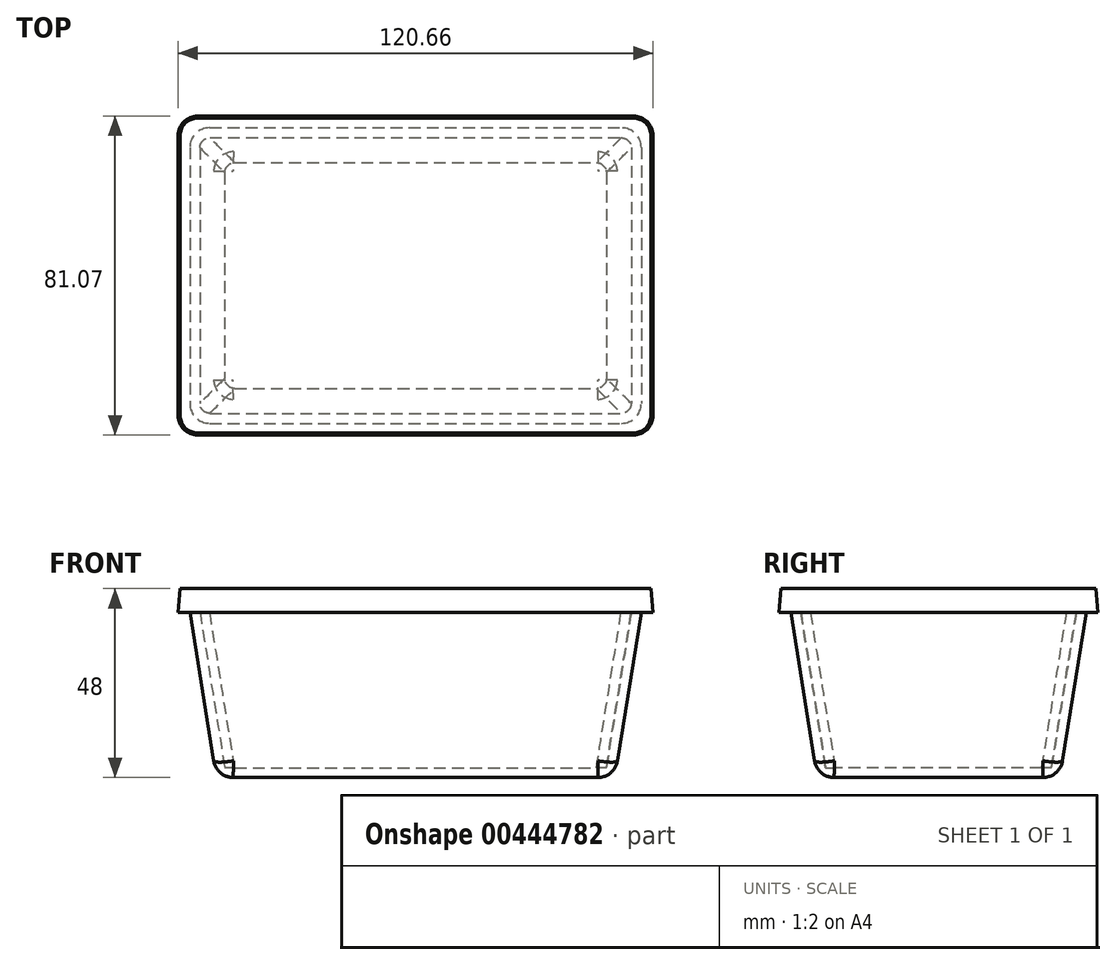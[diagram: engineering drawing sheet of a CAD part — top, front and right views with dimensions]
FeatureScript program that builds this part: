
annotation { "Feature Type Name" : "Feature", "Feature Type Description" : "" }
export const myFeature = defineFeature(function(context is Context, id is Id, definition is map)
    precondition{}
    {
        {
            var Q0;
            Q0=qCreatedBy(makeId("Top.planeOp"),FACE);
            var sketch = newSketch(context, id + "F0", { "sketchPlane" : qUnion([Q0])});
            skLineSegment(sketch, "E0.bottom", {"start": v(-49.28, 19.44) * mm, "end": v(41.94, 19.44) * mm});
            skLineSegment(sketch, "E0.top", {"start": v(-49.28, -42.19) * mm, "end": v(41.94, -42.19) * mm});
            skLineSegment(sketch, "E0.left", {"start": v(-54.28, 14.44) * mm, "end": v(-54.28, -37.19) * mm});
            skLineSegment(sketch, "E0.right", {"start": v(46.94, 14.44) * mm, "end": v(46.94, -37.19) * mm});
            skPoint(sketch, "E1.visualSharp", {"position": v(-54.28, 19.44) * mm});
            skArc(sketch, "E1.filletArc", {"start": v(-49.28, 19.44) * mm, "mid": v(-52.81, 17.98) * mm, "end": v(-54.28, 14.44) * mm});
            skPoint(sketch, "E2.visualSharp", {"position": v(-54.28, -42.19) * mm});
            skArc(sketch, "E2.filletArc", {"start": v(-54.28, -37.19) * mm, "mid": v(-52.81, -40.72) * mm, "end": v(-49.28, -42.19) * mm});
            skPoint(sketch, "E3.visualSharp", {"position": v(46.94, -42.19) * mm});
            skArc(sketch, "E3.filletArc", {"start": v(41.94, -42.19) * mm, "mid": v(45.48, -40.72) * mm, "end": v(46.94, -37.19) * mm});
            skPoint(sketch, "E4.visualSharp", {"position": v(46.94, 19.44) * mm});
            skArc(sketch, "E4.filletArc", {"start": v(46.94, 14.44) * mm, "mid": v(45.48, 17.98) * mm, "end": v(41.94, 19.44) * mm});
            skSolve(sketch);
        }
        {
            var Q0;
            Q0=qCreatedBy(makeId("Top.planeOp"),FACE);
            cPlane(context, id + "F1", {"entities" : qUnion([Q0]), "cplaneType" : CPlaneType.OFFSET, "offset" : 42 * mm, "width" : 150 * mm, "height" : 150 * mm});
        }
        {
            var Q0;
            Q0=qCreatedBy(id+"F1.planeOp",FACE);
            var sketch = newSketch(context, id + "F2", { "sketchPlane" : qUnion([Q0])});
            skLineSegment(sketch, "E5.bottom", {"start": v(-56, 26.16) * mm, "end": v(48.66, 26.16) * mm});
            skLineSegment(sketch, "E5.top", {"start": v(-56, -48.9) * mm, "end": v(48.66, -48.9) * mm});
            skLineSegment(sketch, "E5.left", {"start": v(-61, 21.16) * mm, "end": v(-61, -43.9) * mm});
            skLineSegment(sketch, "E5.right", {"start": v(53.66, 21.16) * mm, "end": v(53.66, -43.9) * mm});
            skPoint(sketch, "E6.visualSharp", {"position": v(-61, 26.16) * mm});
            skArc(sketch, "E6.filletArc", {"start": v(-56, 26.16) * mm, "mid": v(-59.53, 24.7) * mm, "end": v(-61, 21.16) * mm});
            skPoint(sketch, "E7.visualSharp", {"position": v(-61, -48.9) * mm});
            skArc(sketch, "E7.filletArc", {"start": v(-61, -43.9) * mm, "mid": v(-59.53, -47.44) * mm, "end": v(-56, -48.9) * mm});
            skPoint(sketch, "E8.visualSharp", {"position": v(53.66, -48.9) * mm});
            skArc(sketch, "E8.filletArc", {"start": v(48.66, -48.9) * mm, "mid": v(52.2, -47.44) * mm, "end": v(53.66, -43.9) * mm});
            skPoint(sketch, "E9.visualSharp", {"position": v(53.66, 26.16) * mm});
            skArc(sketch, "E9.filletArc", {"start": v(53.66, 21.16) * mm, "mid": v(52.2, 24.7) * mm, "end": v(48.66, 26.16) * mm});
            skSolve(sketch);
        }
        {
            var Q0;
            Q0=makeQuery(id+"F2.imprint","IMPRINT",FACE,{"disambiguationData":[TD([[makeQuery(id+"F2.imprint","IMPRINT",EDGE,{"derivedFrom":sQuery(id+"F2.wireOp",EDGE,"E5.bottom")}),-1.0]])]});
            var Q1;
            Q1=makeQuery(id+"F0.imprint","IMPRINT",FACE,{"disambiguationData":[TD([[makeQuery(id+"F0.imprint","IMPRINT",EDGE,{"derivedFrom":sQuery(id+"F0.wireOp",EDGE,"E0.bottom")}),-1.0]])]});
            loft(context, id + "F3", {"sheetProfilesArray" : [{ "sheetProfileEntities" : qUnion([Q0]) }, { "sheetProfileEntities" : qUnion([Q1]) }]});
        }
        {
            var Q0;
            Q0=makeQuery(id+"F3.opLoft","CAP_FACE",FACE,{"disambiguationData":[OSD([makeQuery(id+"F2.imprint","IMPRINT",FACE,{"disambiguationData":[TD([[makeQuery(id+"F2.imprint","IMPRINT",EDGE,{"derivedFrom":sQuery(id+"F2.wireOp",EDGE,"E5.bottom")}),-1.0]])]})])],"isStart":true});
            shell(context, id + "F4", {"entities" : qUnion([Q0]), "thickness" : 2.5 * mm});
        }
        {
            var Q0;
            Q0=makeQuery(id+"F3.opLoft","CAP_FACE",FACE,{"disambiguationData":[OSD([makeQuery(id+"F2.imprint","IMPRINT",FACE,{"disambiguationData":[TD([[makeQuery(id+"F2.imprint","IMPRINT",EDGE,{"derivedFrom":sQuery(id+"F2.wireOp",EDGE,"E5.bottom")}),-1.0]])]})])],"isStart":true});
            var sketch = newSketch(context, id + "F5", { "sketchPlane" : qUnion([Q0])});
            skLineSegment(sketch, "E10.bottom", {"start": v(-59, 29.16) * mm, "end": v(51.66, 29.16) * mm});
            skLineSegment(sketch, "E10.top", {"start": v(-59, -51.9) * mm, "end": v(51.66, -51.9) * mm});
            skLineSegment(sketch, "E10.left", {"start": v(-64, 24.16) * mm, "end": v(-64, -46.9) * mm});
            skLineSegment(sketch, "E10.right", {"start": v(56.66, 24.16) * mm, "end": v(56.66, -46.9) * mm});
            skPoint(sketch, "E11.visualSharp", {"position": v(-64, 29.16) * mm});
            skArc(sketch, "E11.filletArc", {"start": v(-59, 29.16) * mm, "mid": v(-62.53, 27.7) * mm, "end": v(-64, 24.16) * mm});
            skPoint(sketch, "E12.visualSharp", {"position": v(-64, -51.9) * mm});
            skArc(sketch, "E12.filletArc", {"start": v(-64, -46.9) * mm, "mid": v(-62.53, -50.44) * mm, "end": v(-59, -51.9) * mm});
            skPoint(sketch, "E13.visualSharp", {"position": v(56.66, -51.9) * mm});
            skArc(sketch, "E13.filletArc", {"start": v(51.66, -51.9) * mm, "mid": v(55.2, -50.44) * mm, "end": v(56.66, -46.9) * mm});
            skPoint(sketch, "E14.visualSharp", {"position": v(56.66, 29.16) * mm});
            skArc(sketch, "E14.filletArc", {"start": v(56.66, 24.16) * mm, "mid": v(55.2, 27.7) * mm, "end": v(51.66, 29.16) * mm});
            skSolve(sketch);
        }
        {
            var Q0;
            Q0 = qSketchRegion(id + "F5", true);
            extrude(context, id + "F6", {"entities" : qUnion([Q0]), "operationType" : NewBodyOperationType.ADD, "depth" : 6 * mm, "hasDraft" : true, "draftAngle" : 5 * degree, "draftPullDirection" : true});
        }
        {
            var Q0;
            Q0=makeQuery(id+"F3.opLoft","MID_CAP_EDGE",EDGE,{"disambiguationData":[OSD([sQuery(id+"F0.wireOp",EDGE,"E0.top"),sQuery(id+"F0.wireOp",EDGE,"E0.right"),sQuery(id+"F0.wireOp",EDGE,"E3.filletArc")])],"capPos":1.0});
            fillet(context, id + "F7", {"entities" : qUnion([Q0]), "radius" : 5 * mm, "tangentPropagation" : true, "allowEdgeOverflow" : false});
        }
    });
